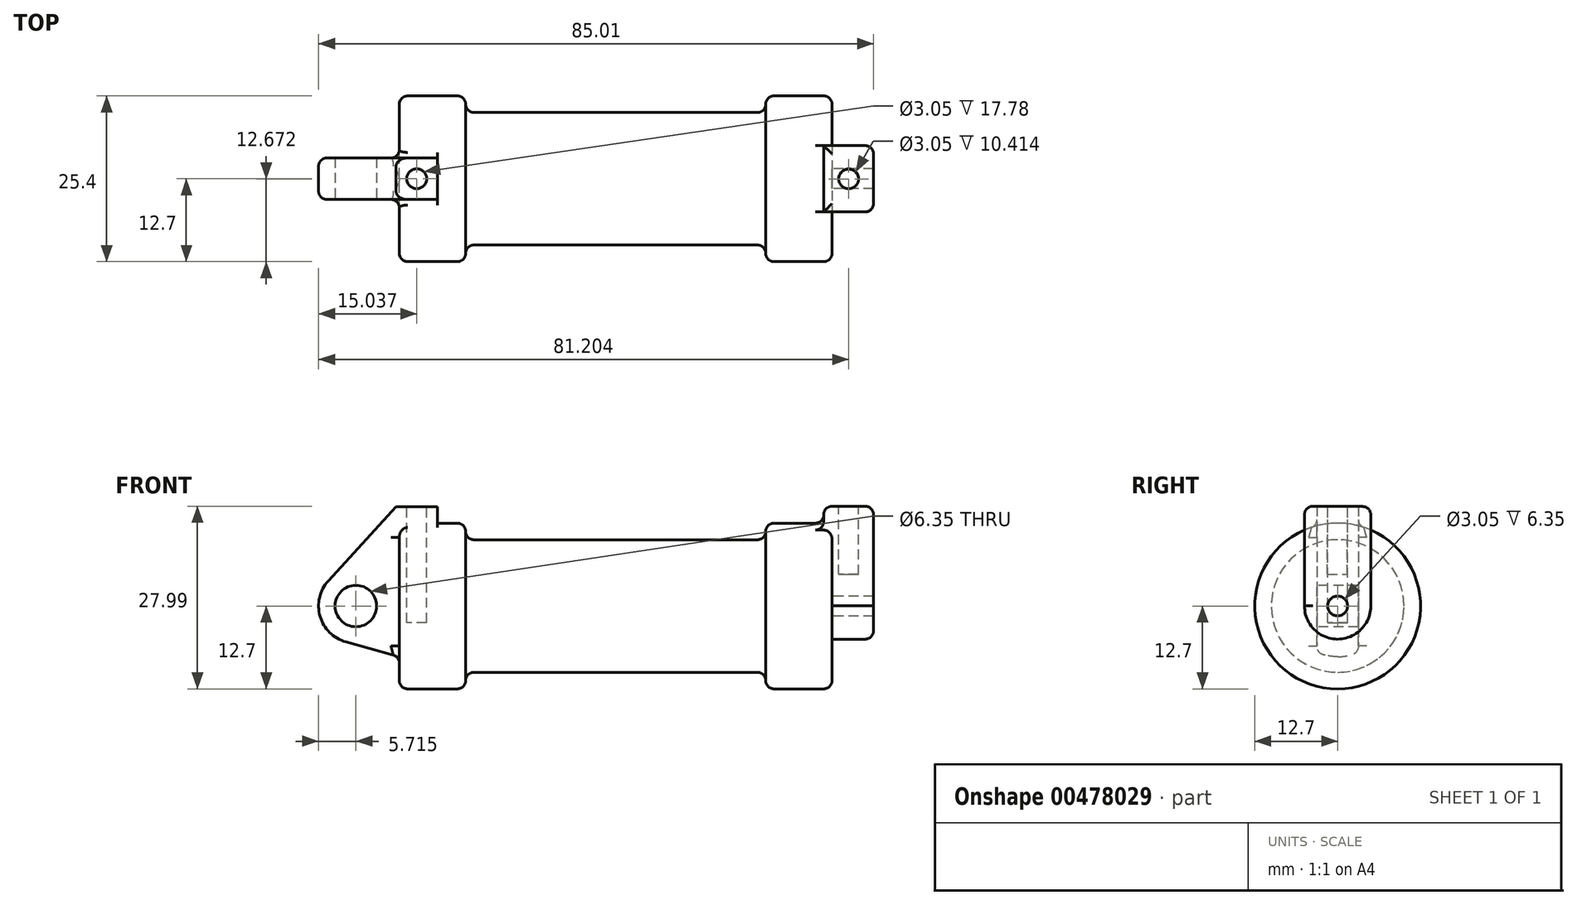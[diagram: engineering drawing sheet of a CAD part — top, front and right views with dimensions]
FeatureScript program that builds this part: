
annotation { "Feature Type Name" : "Feature", "Feature Type Description" : "" }
export const myFeature = defineFeature(function(context is Context, id is Id, definition is map)
    precondition{}
    {
        {
            var Q0;
            Q0=qCreatedBy(makeId("Front.planeOp"),FACE);
            var sketch = newSketch(context, id + "F0", { "sketchPlane" : qUnion([Q0])});
            skLineSegment(sketch, "E0", {"start": v(0, 0) * mm, "end": v(0, 12.7) * mm});
            skLineSegment(sketch, "E1", {"start": v(0, 12.7) * mm, "end": v(10.16, 12.7) * mm});
            skLineSegment(sketch, "E2", {"start": v(10.16, 12.7) * mm, "end": v(10.16, 10.16) * mm});
            skLineSegment(sketch, "E3", {"start": v(10.16, 10.16) * mm, "end": v(56.13, 10.16) * mm});
            skLineSegment(sketch, "E4", {"start": v(56.13, 10.16) * mm, "end": v(56.13, 12.7) * mm});
            skLineSegment(sketch, "E5", {"start": v(56.13, 12.7) * mm, "end": v(66.3, 12.7) * mm});
            skLineSegment(sketch, "E6", {"start": v(66.3, 12.7) * mm, "end": v(66.3, 0) * mm});
            skLineSegment(sketch, "E7", {"start": v(66.3, 0) * mm, "end": v(0, 0) * mm});
            skLineSegment(sketch, "E8", {"start": v(5.84, 15.24) * mm, "end": v(-0.5, 15.24) * mm});
            skLineSegment(sketch, "E9", {"start": v(-0.5, 15.24) * mm, "end": v(-10.88, 3.85) * mm});
            skLineSegment(sketch, "E10", {"start": v(0, 0) * mm, "end": v(-6.65, 0) * mm});
            skCircle(sketch, "E11", {"center": v(-6.65, 0) * mm, "radius": 5.72 * mm});
            skCircle(sketch, "E12", {"center": v(-6.65, 0) * mm, "radius": 3.18 * mm});
            skLineSegment(sketch, "E13", {"start": v(5.84, 15.24) * mm, "end": v(5.84, -9.4) * mm});
            skLineSegment(sketch, "E14", {"start": v(5.84, -9.4) * mm, "end": v(-8.18, -5.5) * mm});
            skSolve(sketch);
        }
        {
            var Q0;
            {var subQ0=sQuery(id+"F0.wireOp",EDGE,"E2");Q0=makeQuery(id+"F0.imprint","IMPRINT",FACE,{"disambiguationData":[TD([[makeQuery(id+"F0.imprint","IMPRINT",EDGE,{"derivedFrom":subQ0}),-1.0]])]});}
            var Q1;
            {var subQ0=sQuery(id+"F0.wireOp",EDGE,"E0");Q1=makeQuery(id+"F0.imprint","IMPRINT",FACE,{"disambiguationData":[TD([[makeQuery(id+"F0.imprint","IMPRINT",EDGE,{"derivedFrom":subQ0}),-1.0]])]});}
            var Q2;
            Q2=sQuery(id+"F0.wireOp",EDGE,"E7");
            revolve(context, id + "F1", {"entities" : qUnion([Q0, Q1]), "axis" : qUnion([Q2]), "revolveType" : RevolveType.FULL});
        }
        {
            var Q0;
            {var subQ0=sQuery(id+"F0.wireOp",EDGE,"E0");Q0=makeQuery(id+"F0.imprint","IMPRINT",FACE,{"disambiguationData":[TD([[makeQuery(id+"F0.imprint","IMPRINT",EDGE,{"derivedFrom":subQ0}),-1.0]])]});}
            var Q1;
            {var subQ1=sQuery(id+"F0.wireOp",EDGE,"E0");Q1=makeQuery(id+"F0.imprint","IMPRINT",FACE,{"disambiguationData":[TD([[makeQuery(id+"F0.imprint","IMPRINT",EDGE,{"derivedFrom":subQ1}),1.0]])]});}
            var Q2;
            {var subQ5=sQuery(id+"F0.wireOp",EDGE,"E12");Q2=makeQuery(id+"F0.imprint","IMPRINT",FACE,{"disambiguationData":[TD([[makeQuery(id+"F0.imprint","IMPRINT",EDGE,{"derivedFrom":subQ5}),-1.0]])]});}
            var Q3;
            {var subQ0=sQuery(id+"F0.wireOp",EDGE,"E14");Q3=makeQuery(id+"F0.imprint","IMPRINT",FACE,{"disambiguationData":[TD([[makeQuery(id+"F0.imprint","IMPRINT",EDGE,{"derivedFrom":subQ0}),-1.0]])]});}
            extrude(context, id + "F2", {"entities" : qUnion([Q0, Q1, Q2, Q3]), "operationType" : NewBodyOperationType.ADD, "oppositeDirection" : true, "depth" : 6.35 * mm, "symmetric" : true});
        }
        {
            var Q0;
            Q0=makeQuery(id+"F1.opRevolve","SWEPT_FACE",FACE,{"disambiguationData":[OSD([sQuery(id+"F0.wireOp",EDGE,"E6")])]});
            var sketch = newSketch(context, id + "F3", { "sketchPlane" : qUnion([Q0])});
            skCircle(sketch, "E15", {"center": v(0, 0) * mm, "radius": 5.08 * mm});
            skCircle(sketch, "E16", {"center": v(0, 0) * mm, "radius": 1.52 * mm});
            skLineSegment(sketch, "E17", {"start": v(5.08, 0) * mm, "end": v(5.08, 15.24) * mm});
            skLineSegment(sketch, "E18", {"start": v(-5.08, 0.05) * mm, "end": v(-5.08, 15.3) * mm});
            skLineSegment(sketch, "E19", {"start": v(-5.08, 15.3) * mm, "end": v(5.08, 15.24) * mm});
            skSolve(sketch);
        }
        {
            var Q0;
            {var subQ0=sQuery(id+"F3.wireOp",EDGE,"E19");Q0=makeQuery(id+"F3.imprint","IMPRINT",FACE,{"disambiguationData":[TD([[makeQuery(id+"F3.imprint","IMPRINT",EDGE,{"derivedFrom":subQ0}),-1.0]])]});}
            var Q1;
            {var subQ0=sQuery(id+"F3.wireOp",EDGE,"E17");var subQ1=sQuery(id+"F3.wireOp",EDGE,"E15");var subQ2=makeQuery(id+"F3.imprint","INTERSECT",VERTEX,{"derivedFrom":[subQ1,subQ0]});Q1=makeQuery(id+"F3.imprint","IMPRINT",FACE,{"disambiguationData":[TD([[makeQuery(id+"F3.imprint","IMPRINT",EDGE,{"disambiguationData":[TD([[subQ2,-1.0]])],"derivedFrom":subQ1}),-1.0]])]});}
            var Q2;
            Q2=makeQuery(id+"F3.imprint","IMPRINT",FACE,{"disambiguationData":[TD([[makeQuery(id+"F3.imprint","IMPRINT",EDGE,{"derivedFrom":sQuery(id+"F3.wireOp",EDGE,"E16")}),-1.0]])]});
            extrude(context, id + "F4", {"entities" : qUnion([Q0, Q1, Q2]), "operationType" : NewBodyOperationType.ADD, "oppositeDirection" : true, "depth" : 1.27 * mm});
        }
        {
            var Q0;
            Q0 = qSketchRegion(id + "F3", true);
            extrude(context, id + "F5", {"entities" : qUnion([Q0]), "operationType" : NewBodyOperationType.ADD, "depth" : 6.35 * mm});
        }
        {
            var Q0;
            Q0=makeQuery(id+"F2.opExtrude","SWEPT_FACE",FACE,{"disambiguationData":[OSD([sQuery(id+"F0.wireOp",EDGE,"E8")])]});
            var sketch = newSketch(context, id + "F6", { "sketchPlane" : qUnion([Q0])});
            skCircle(sketch, "E20", {"center": v(2.67, 0) * mm, "radius": 1.52 * mm});
            skSolve(sketch);
        }
        {
            var Q0;
            Q0=makeQuery(id+"F6.imprint","IMPRINT",FACE,{"disambiguationData":[TD([[makeQuery(id+"F6.imprint","IMPRINT",EDGE,{"derivedFrom":sQuery(id+"F6.wireOp",EDGE,"E20")}),1.0]])]});
            var Q1;
            Q1=sQuery(id+"F6.wireOp",EDGE,"E20");
            extrude(context, id + "F7", {"entities" : qUnion([Q0]), "operationType" : NewBodyOperationType.REMOVE, "surfaceEntities" : qUnion([Q1]), "oppositeDirection" : true, "depth" : 17.78 * mm});
        }
        {
            var Q0;
            {var subQ0=sQuery(id+"F3.wireOp",EDGE,"E19");Q0=makeQuery(id+"F5.boolean.opBoolean","MERGE",FACE,{"derivedFrom":[makeQuery(id+"F4.opExtrude","SWEPT_FACE",FACE,{"disambiguationData":[OSD([subQ0])]}),makeQuery(id+"F5.opExtrude","SWEPT_FACE",FACE,{"disambiguationData":[OSD([subQ0])]})]});}
            var sketch = newSketch(context, id + "F8", { "sketchPlane" : qUnion([Q0])});
            skCircle(sketch, "E21", {"center": v(68.83, -0.08) * mm, "radius": 1.52 * mm});
            skSolve(sketch);
        }
        {
            var Q0;
            Q0=makeQuery(id+"F8.imprint","IMPRINT",FACE,{"disambiguationData":[TD([[makeQuery(id+"F8.imprint","IMPRINT",EDGE,{"derivedFrom":sQuery(id+"F8.wireOp",EDGE,"E21")}),1.0]])]});
            extrude(context, id + "F9", {"entities" : qUnion([Q0]), "operationType" : NewBodyOperationType.REMOVE, "oppositeDirection" : true, "depth" : 10.4 * mm});
        }
        {
            var Q0;
            Q0=makeQuery(id+"F1.opRevolve","SWEPT_EDGE",EDGE,{"disambiguationData":[OSD([sQuery(id+"F0.wireOp",EDGE,"E1"),sQuery(id+"F0.wireOp",EDGE,"E2")])]});
            var Q1;
            Q1=makeQuery(id+"F1.opRevolve","SWEPT_EDGE",EDGE,{"disambiguationData":[OSD([sQuery(id+"F0.wireOp",EDGE,"E4"),sQuery(id+"F0.wireOp",EDGE,"E5")])]});
            var Q2;
            Q2=makeQuery(id+"F1.opRevolve","SWEPT_EDGE",EDGE,{"disambiguationData":[OSD([sQuery(id+"F0.wireOp",EDGE,"E0"),sQuery(id+"F0.wireOp",EDGE,"E1")])]});
            var Q3;
            Q3=makeQuery(id+"F1.opRevolve","SWEPT_EDGE",EDGE,{"disambiguationData":[OSD([sQuery(id+"F0.wireOp",EDGE,"E5"),sQuery(id+"F0.wireOp",EDGE,"E6")])]});
            fillet(context, id + "F10", {"entities" : qUnion([Q0, Q1, Q2, Q3]), "radius" : 1.27 * mm, "tangentPropagation" : true, "allowEdgeOverflow" : false});
        }
        {
            var Q0;
            Q0=makeQuery(id+"F1.opRevolve","SWEPT_EDGE",EDGE,{"disambiguationData":[OSD([sQuery(id+"F0.wireOp",EDGE,"E2"),sQuery(id+"F0.wireOp",EDGE,"E3")])]});
            var Q1;
            Q1=makeQuery(id+"F1.opRevolve","SWEPT_EDGE",EDGE,{"disambiguationData":[OSD([sQuery(id+"F0.wireOp",EDGE,"E3"),sQuery(id+"F0.wireOp",EDGE,"E4")])]});
            var Q2;
            Q2=makeQuery(id+"F2.opExtrude","CAP_EDGE",EDGE,{"disambiguationData":[OSD([sQuery(id+"F0.wireOp",EDGE,"E14")])],"isStart":true});
            var Q3;
            Q3=makeQuery(id+"F2.opExtrude","CAP_EDGE",EDGE,{"disambiguationData":[OSD([sQuery(id+"F0.wireOp",EDGE,"E11")])],"isStart":true});
            var Q4;
            Q4=makeQuery(id+"F2.boolean.opBoolean","INTERSECT",EDGE,{"derivedFrom":[makeQuery(id+"F1.opRevolve","SWEPT_FACE",FACE,{"disambiguationData":[OSD([sQuery(id+"F0.wireOp",EDGE,"E0")])]}),makeQuery(id+"F2.opExtrude","CAP_FACE",FACE,{"disambiguationData":[OSD([sQuery(id+"F0.wireOp",EDGE,"E8"),sQuery(id+"F0.wireOp",EDGE,"E9"),sQuery(id+"F0.wireOp",EDGE,"E11"),sQuery(id+"F0.wireOp",EDGE,"E12"),sQuery(id+"F0.wireOp",EDGE,"E13"),sQuery(id+"F0.wireOp",EDGE,"E14")])],"isStart":true})]});
            var Q5;
            Q5=makeQuery(id+"F2.opExtrude","CAP_EDGE",EDGE,{"disambiguationData":[OSD([sQuery(id+"F0.wireOp",EDGE,"E9")])],"isStart":false});
            var Q6;
            Q6=makeQuery(id+"F2.boolean.opBoolean","INTERSECT",EDGE,{"derivedFrom":[makeQuery(id+"F1.opRevolve","SWEPT_FACE",FACE,{"disambiguationData":[OSD([sQuery(id+"F0.wireOp",EDGE,"E0")])]}),makeQuery(id+"F2.opExtrude","CAP_FACE",FACE,{"disambiguationData":[OSD([sQuery(id+"F0.wireOp",EDGE,"E8"),sQuery(id+"F0.wireOp",EDGE,"E9"),sQuery(id+"F0.wireOp",EDGE,"E11"),sQuery(id+"F0.wireOp",EDGE,"E12"),sQuery(id+"F0.wireOp",EDGE,"E13"),sQuery(id+"F0.wireOp",EDGE,"E14")])],"isStart":false})]});
            fillet(context, id + "F11", {"entities" : qUnion([Q0, Q1, Q2, Q3, Q4, Q5, Q6]), "radius" : 1.27 * mm, "tangentPropagation" : true, "allowEdgeOverflow" : false});
        }
        {
            var Q0;
            Q0=makeQuery(id+"F5.opExtrude","CAP_EDGE",EDGE,{"disambiguationData":[OSD([sQuery(id+"F3.wireOp",EDGE,"E18")])],"isStart":true});
            var Q1;
            {var subQ0=sQuery(id+"F3.wireOp",EDGE,"E19");var subQ1=sQuery(id+"F3.wireOp",EDGE,"E17");Q1=makeQuery(id+"F5.boolean.opBoolean","MERGE",EDGE,{"derivedFrom":[makeQuery(id+"F4.opExtrude","SWEPT_EDGE",EDGE,{"disambiguationData":[OSD([subQ1,subQ0])]}),makeQuery(id+"F5.opExtrude","SWEPT_EDGE",EDGE,{"disambiguationData":[OSD([subQ1,subQ0])]})]});}
            var Q2;
            Q2=makeQuery(id+"F5.opExtrude","CAP_EDGE",EDGE,{"disambiguationData":[OSD([sQuery(id+"F3.wireOp",EDGE,"E17")])],"isStart":true});
            var Q3;
            Q3=makeQuery(id+"F4.boolean.opBoolean","INTERSECT",EDGE,{"derivedFrom":[makeQuery(id+"F1.opRevolve","SWEPT_FACE",FACE,{"disambiguationData":[OSD([sQuery(id+"F0.wireOp",EDGE,"E5")])]}),makeQuery(id+"F4.opExtrude","CAP_FACE",FACE,{"disambiguationData":[OSD([sQuery(id+"F3.wireOp",EDGE,"E15"),sQuery(id+"F3.wireOp",EDGE,"E16"),sQuery(id+"F3.wireOp",EDGE,"E17"),sQuery(id+"F3.wireOp",EDGE,"E18"),sQuery(id+"F3.wireOp",EDGE,"E19")])],"isStart":false})]});
            var Q4;
            Q4=makeQuery(id+"F4.opExtrude","CAP_EDGE",EDGE,{"disambiguationData":[OSD([sQuery(id+"F3.wireOp",EDGE,"E19")])],"isStart":false});
            var Q5;
            Q5=makeQuery(id+"F5.opExtrude","CAP_EDGE",EDGE,{"disambiguationData":[OSD([sQuery(id+"F3.wireOp",EDGE,"E17")])],"isStart":false});
            var Q6;
            Q6=makeQuery(id+"F5.opExtrude","CAP_EDGE",EDGE,{"disambiguationData":[OSD([sQuery(id+"F3.wireOp",EDGE,"E19")])],"isStart":false});
            var Q7;
            {var subQ0=sQuery(id+"F3.wireOp",EDGE,"E19");var subQ1=sQuery(id+"F3.wireOp",EDGE,"E18");Q7=makeQuery(id+"F5.boolean.opBoolean","MERGE",EDGE,{"derivedFrom":[makeQuery(id+"F4.opExtrude","SWEPT_EDGE",EDGE,{"disambiguationData":[OSD([subQ1,subQ0])]}),makeQuery(id+"F5.opExtrude","SWEPT_EDGE",EDGE,{"disambiguationData":[OSD([subQ1,subQ0])]})]});}
            fillet(context, id + "F12", {"entities" : qUnion([Q0, Q1, Q2, Q3, Q4, Q5, Q6, Q7]), "radius" : 1.27 * mm, "tangentPropagation" : true, "allowEdgeOverflow" : false});
        }
    });
